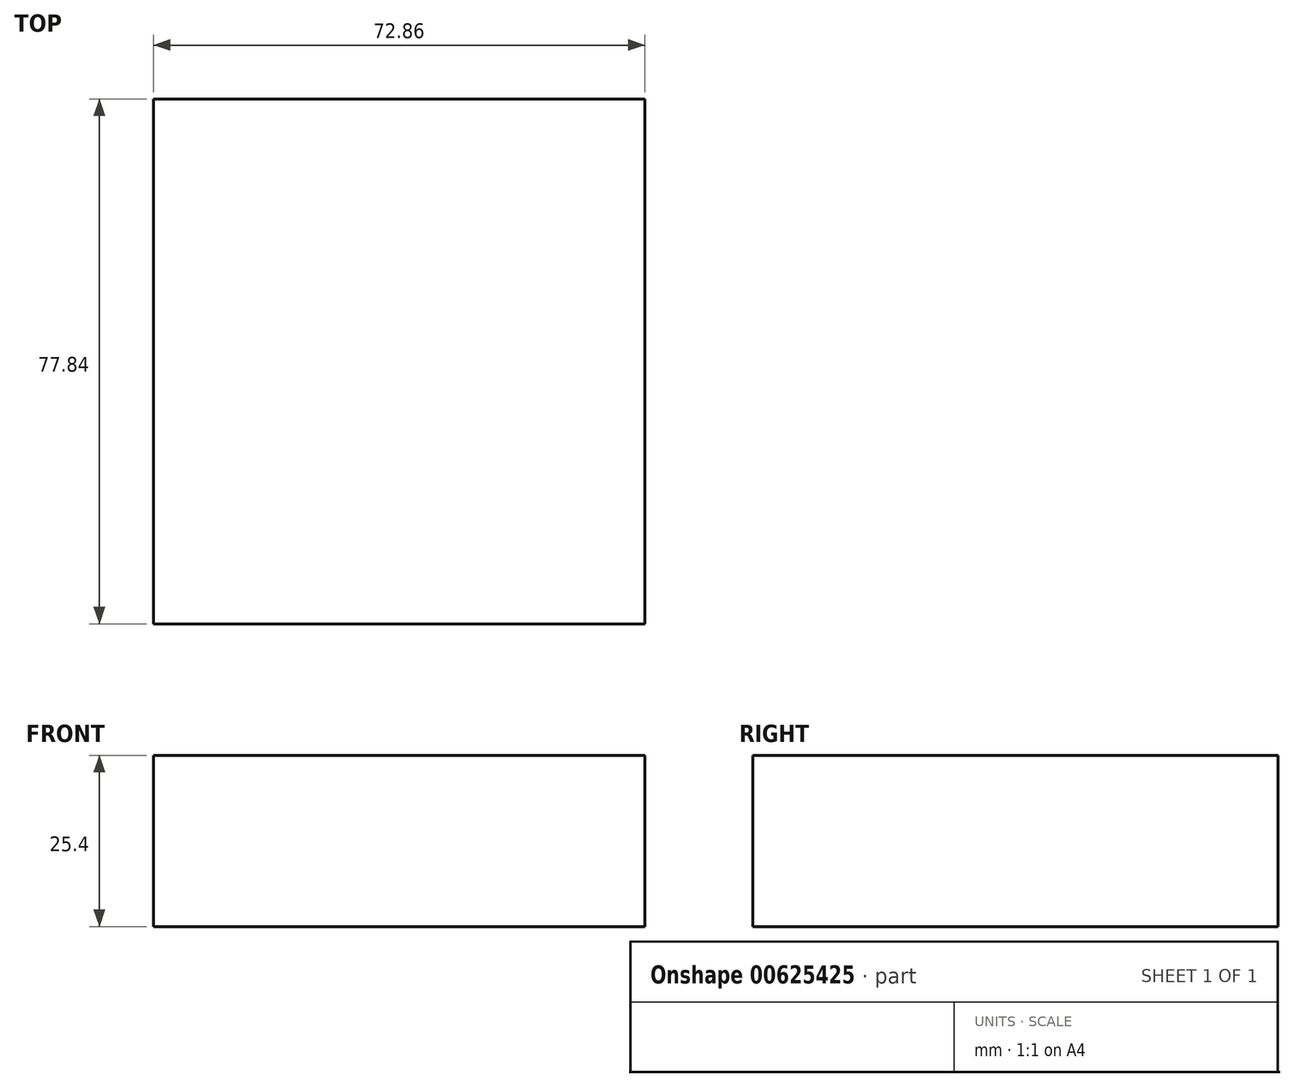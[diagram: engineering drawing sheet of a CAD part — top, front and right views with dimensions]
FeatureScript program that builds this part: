
annotation { "Feature Type Name" : "Feature", "Feature Type Description" : "" }
export const myFeature = defineFeature(function(context is Context, id is Id, definition is map)
    precondition{}
    {
        {
            var Q0;
            Q0=qCreatedBy(makeId("Top.planeOp"),FACE);
            var sketch = newSketch(context, id + "F0", { "sketchPlane" : qUnion([Q0])});
            skLineSegment(sketch, "E0.bottom", {"start": v(-36.43, 38.92) * mm, "end": v(36.43, 38.92) * mm});
            skLineSegment(sketch, "E0.top", {"start": v(-36.43, -38.92) * mm, "end": v(36.43, -38.92) * mm});
            skLineSegment(sketch, "E0.left", {"start": v(-36.43, 38.92) * mm, "end": v(-36.43, -38.92) * mm});
            skLineSegment(sketch, "E0.right", {"start": v(36.43, 38.92) * mm, "end": v(36.43, -38.92) * mm});
            skPoint(sketch, "E0.middle", {"position": v(0, 0) * mm});
            skSolve(sketch);
        }
        {
            var Q0;
            Q0 = qSketchRegion(id + "F0", true);
            extrude(context, id + "F1", {"entities" : qUnion([Q0]), "depth" : 25.4 * mm, "offsetDistance" : 25.4 * mm});
        }
    });
